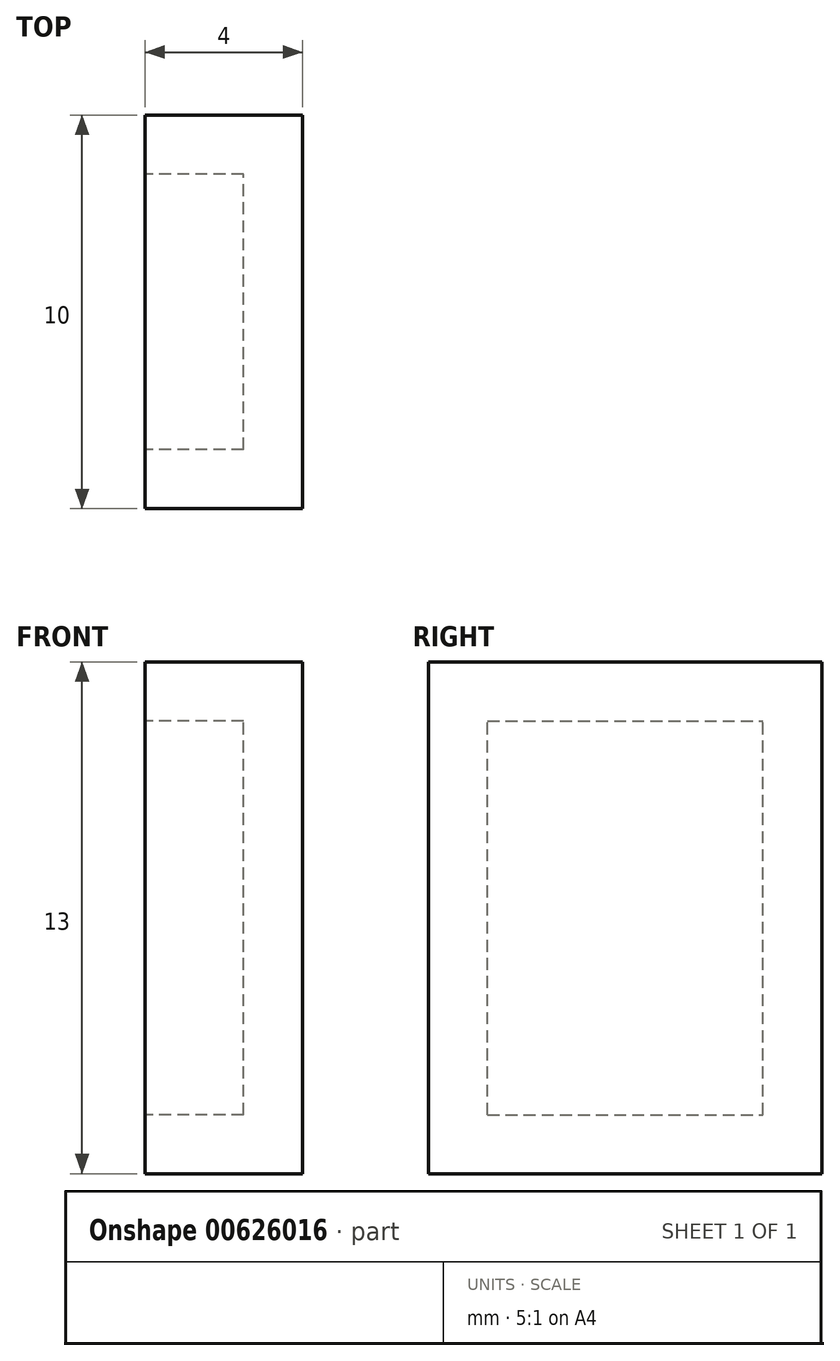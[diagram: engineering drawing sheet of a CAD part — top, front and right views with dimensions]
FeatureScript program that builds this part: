
annotation { "Feature Type Name" : "Feature", "Feature Type Description" : "" }
export const myFeature = defineFeature(function(context is Context, id is Id, definition is map)
    precondition{}
    {
        {
            var Q0;
            Q0=qCreatedBy(makeId("Right.planeOp"),FACE);
            var sketch = newSketch(context, id + "F0", { "sketchPlane" : qUnion([Q0])});
            skLineSegment(sketch, "E0.bottom", {"start": v(0, 0) * mm, "end": v(10, 0) * mm});
            skLineSegment(sketch, "E0.top", {"start": v(0, 13) * mm, "end": v(10, 13) * mm});
            skLineSegment(sketch, "E0.left", {"start": v(0, 0) * mm, "end": v(0, 13) * mm});
            skLineSegment(sketch, "E0.right", {"start": v(10, 0) * mm, "end": v(10, 13) * mm});
            skSolve(sketch);
        }
        {
            var Q0;
            Q0=makeQuery(id+"F0.imprint","IMPRINT",FACE,{"disambiguationData":[TD([[makeQuery(id+"F0.imprint","IMPRINT",EDGE,{"derivedFrom":sQuery(id+"F0.wireOp",EDGE,"E0.bottom")}),1.0]])]});
            extrude(context, id + "F1", {"entities" : qUnion([Q0]), "depth" : 4 * mm, "offsetDistance" : 25 * mm});
        }
        {
            var Q0;
            Q0=makeQuery(id+"F1.opExtrude","CAP_FACE",FACE,{"disambiguationData":[OSD([sQuery(id+"F0.wireOp",EDGE,"E0.bottom"),sQuery(id+"F0.wireOp",EDGE,"E0.top"),sQuery(id+"F0.wireOp",EDGE,"E0.left"),sQuery(id+"F0.wireOp",EDGE,"E0.right")])],"isStart":true});
            shell(context, id + "F2", {"entities" : qUnion([Q0]), "thickness" : 1.5 * mm});
        }
    });
